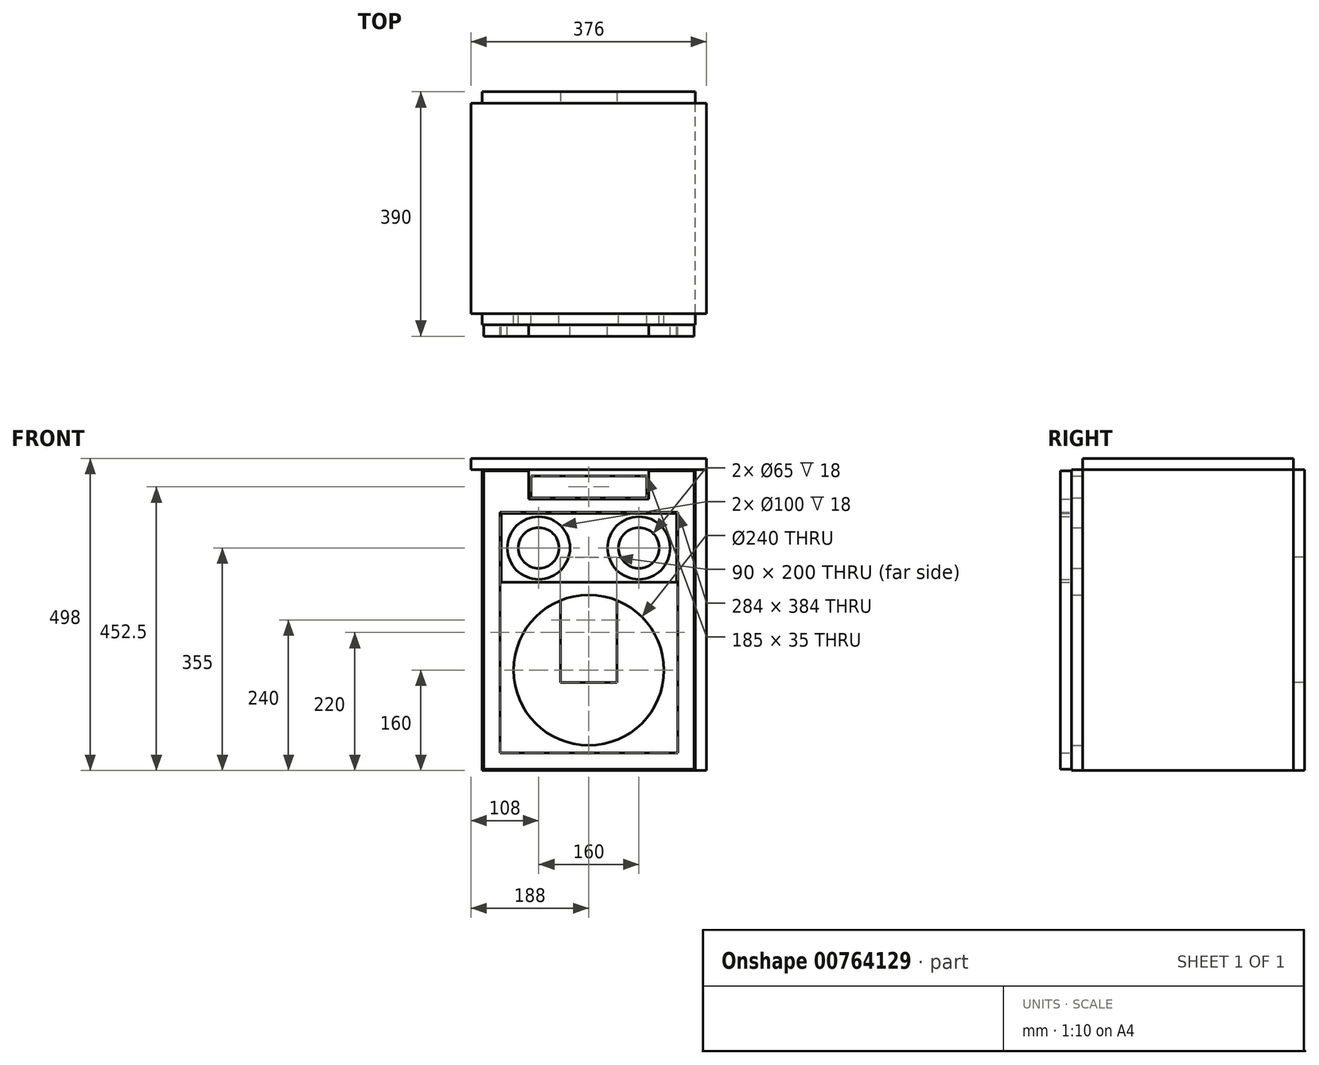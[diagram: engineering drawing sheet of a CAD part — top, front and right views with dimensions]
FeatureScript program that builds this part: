
annotation { "Feature Type Name" : "Feature", "Feature Type Description" : "" }
export const myFeature = defineFeature(function(context is Context, id is Id, definition is map)
    precondition{}
    {
        {
            var Q0;
            Q0=qCreatedBy(makeId("Front.planeOp"),FACE);
            var sketch = newSketch(context, id + "F0", { "sketchPlane" : qUnion([Q0])});
            skLineSegment(sketch, "E0.bottom", {"start": v(170, -240) * mm, "end": v(-170, -240) * mm});
            skLineSegment(sketch, "E0.top", {"start": v(170, 240) * mm, "end": v(-170, 240) * mm});
            skLineSegment(sketch, "E0.left", {"start": v(170, -240) * mm, "end": v(170, 240) * mm});
            skLineSegment(sketch, "E0.right", {"start": v(-170, -240) * mm, "end": v(-170, 240) * mm});
            skPoint(sketch, "E0.middle", {"position": v(0, 0) * mm});
            skLineSegment(sketch, "E1", {"start": v(0, 240) * mm, "end": v(0, -240) * mm, "construction": true});
            skCircle(sketch, "E2", {"center": v(0, -80) * mm, "radius": 120 * mm});
            skCircle(sketch, "E3", {"center": v(-80, 115) * mm, "radius": 32.5 * mm});
            skCircle(sketch, "E4", {"center": v(80, 115) * mm, "radius": 32.5 * mm});
            skLineSegment(sketch, "E5.bottom", {"start": v(92.5, 195) * mm, "end": v(-92.5, 195) * mm});
            skLineSegment(sketch, "E5.top", {"start": v(92.5, 230) * mm, "end": v(-92.5, 230) * mm});
            skLineSegment(sketch, "E5.left", {"start": v(92.5, 195) * mm, "end": v(92.5, 230) * mm});
            skLineSegment(sketch, "E5.right", {"start": v(-92.5, 195) * mm, "end": v(-92.5, 230) * mm});
            skPoint(sketch, "E5.middle", {"position": v(0, 212.5) * mm});
            skSolve(sketch);
        }
        {
            var Q0;
            Q0 = qSketchRegion(id + "F0", true);
            extrude(context, id + "F1", {"entities" : qUnion([Q0]), "depth" : 18 * mm, "offsetDistance" : 25 * mm});
        }
        {
            var Q0;
            Q0=makeQuery(id+"F1.opExtrude","CAP_FACE",FACE,{"disambiguationData":[OSD([sQuery(id+"F0.wireOp",EDGE,"E0.bottom"),sQuery(id+"F0.wireOp",EDGE,"E0.top"),sQuery(id+"F0.wireOp",EDGE,"E0.left"),sQuery(id+"F0.wireOp",EDGE,"E0.right"),sQuery(id+"F0.wireOp",EDGE,"E2")])],"isStart":false});
            var sketch = newSketch(context, id + "F2", { "sketchPlane" : qUnion([Q0])});
            skLineSegment(sketch, "E6.bottom", {"start": v(-140, 60) * mm, "end": v(140, 60) * mm});
            skLineSegment(sketch, "E6.top", {"start": v(-140, 170) * mm, "end": v(140, 170) * mm});
            skLineSegment(sketch, "E6.left", {"start": v(-140, 60) * mm, "end": v(-140, 170) * mm});
            skLineSegment(sketch, "E6.right", {"start": v(140, 60) * mm, "end": v(140, 170) * mm});
            skCircle(sketch, "E7", {"center": v(-80, 115) * mm, "radius": 50 * mm});
            skPoint(sketch, "E7.centerSnap0", {"position": v(-140, 115) * mm});
            skCircle(sketch, "E8", {"center": v(80, 115) * mm, "radius": 50 * mm});
            skPoint(sketch, "E8.centerSnap0", {"position": v(140, 115) * mm});
            skSolve(sketch);
        }
        {
            var Q0;
            Q0 = qSketchRegion(id + "F2", true);
            extrude(context, id + "F3", {"entities" : qUnion([Q0]), "operationType" : NewBodyOperationType.ADD, "depth" : 18 * mm, "offsetDistance" : 25 * mm});
        }
        {
            var Q0;
            Q0=makeQuery(id+"F1.opExtrude","CAP_FACE",FACE,{"disambiguationData":[OSD([sQuery(id+"F0.wireOp",EDGE,"E0.bottom"),sQuery(id+"F0.wireOp",EDGE,"E0.top"),sQuery(id+"F0.wireOp",EDGE,"E0.left"),sQuery(id+"F0.wireOp",EDGE,"E0.right"),sQuery(id+"F0.wireOp",EDGE,"E2"),sQuery(id+"F0.wireOp",EDGE,"E3"),sQuery(id+"F0.wireOp",EDGE,"E4")])],"isStart":false});
            var sketch = newSketch(context, id + "F4", { "sketchPlane" : qUnion([Q0])});
            skLineSegment(sketch, "E9.top", {"start": v(-168, -238) * mm, "end": v(168, -238) * mm});
            skLineSegment(sketch, "E9.left", {"start": v(-168, 238) * mm, "end": v(-168, -238) * mm});
            skLineSegment(sketch, "E9.right", {"start": v(168, 238) * mm, "end": v(168, -238) * mm});
            skLineSegment(sketch, "E10", {"start": v(-168, 238) * mm, "end": v(-96, 238) * mm});
            skLineSegment(sketch, "E11", {"start": v(-96, 238) * mm, "end": v(-96, 193) * mm});
            skLineSegment(sketch, "E12", {"start": v(-96, 193) * mm, "end": v(96, 193) * mm});
            skLineSegment(sketch, "E13", {"start": v(96, 193) * mm, "end": v(96, 238) * mm});
            skLineSegment(sketch, "E14", {"start": v(96, 238) * mm, "end": v(168, 238) * mm});
            skLineSegment(sketch, "E15.bottom", {"start": v(-142, 172) * mm, "end": v(142, 172) * mm});
            skLineSegment(sketch, "E15.top", {"start": v(-142, -212) * mm, "end": v(142, -212) * mm});
            skLineSegment(sketch, "E15.left", {"start": v(-142, 172) * mm, "end": v(-142, -212) * mm});
            skLineSegment(sketch, "E15.right", {"start": v(142, 172) * mm, "end": v(142, -212) * mm});
            skSolve(sketch);
        }
        {
            var Q0;
            Q0 = qSketchRegion(id + "F4", true);
            extrude(context, id + "F5", {"entities" : qUnion([Q0]), "depth" : 18 * mm, "offsetDistance" : 25 * mm});
        }
        {
            var Q0;
            Q0=makeQuery(id+"F1.opExtrude","SWEPT_FACE",FACE,{"disambiguationData":[OSD([sQuery(id+"F0.wireOp",EDGE,"E0.left")])]});
            var sketch = newSketch(context, id + "F6", { "sketchPlane" : qUnion([Q0])});
            skLineSegment(sketch, "E16.bottom", {"start": v(0, 240) * mm, "end": v(336, 240) * mm});
            skLineSegment(sketch, "E16.top", {"start": v(0, -240) * mm, "end": v(336, -240) * mm});
            skLineSegment(sketch, "E16.left", {"start": v(0, 240) * mm, "end": v(0, -240) * mm});
            skLineSegment(sketch, "E16.right", {"start": v(336, 240) * mm, "end": v(336, -240) * mm});
            skSolve(sketch);
        }
        {
            var Q0;
            Q0 = qSketchRegion(id + "F6", true);
            extrude(context, id + "F7", {"entities" : qUnion([Q0]), "depth" : 18 * mm, "offsetDistance" : 25 * mm});
        }
        {
            var Q0;
            Q0=makeQuery(id+"F1.opExtrude","CAP_FACE",FACE,{"disambiguationData":[OSD([sQuery(id+"F0.wireOp",EDGE,"E0.bottom"),sQuery(id+"F0.wireOp",EDGE,"E0.top"),sQuery(id+"F0.wireOp",EDGE,"E0.left"),sQuery(id+"F0.wireOp",EDGE,"E0.right"),sQuery(id+"F0.wireOp",EDGE,"E2"),sQuery(id+"F0.wireOp",EDGE,"E3"),sQuery(id+"F0.wireOp",EDGE,"E4")])],"isStart":true});
            var sketch = newSketch(context, id + "F8", { "sketchPlane" : qUnion([Q0])});
            skLineSegment(sketch, "E17.bottom", {"start": v(-170, 240) * mm, "end": v(170, 240) * mm});
            skLineSegment(sketch, "E17.top", {"start": v(-170, -240) * mm, "end": v(170, -240) * mm});
            skLineSegment(sketch, "E17.left", {"start": v(-170, 240) * mm, "end": v(-170, -240) * mm});
            skLineSegment(sketch, "E17.right", {"start": v(170, 240) * mm, "end": v(170, -240) * mm});
            skSolve(sketch);
        }
        {
            var Q0;
            Q0 = qSketchRegion(id + "F8", true);
            extrude(context, id + "F9", {"entities" : qUnion([Q0]), "depth" : 18 * mm, "offsetDistance" : 25 * mm});
        }
        {
            var Q0;
            Q0=makeQuery(id+"F9.opExtrude","SWEPT_BODY",BODY,{"disambiguationData":[OSD([sQuery(id+"F8.wireOp",EDGE,"E17.bottom"),sQuery(id+"F8.wireOp",EDGE,"E17.top"),sQuery(id+"F8.wireOp",EDGE,"E17.left"),sQuery(id+"F8.wireOp",EDGE,"E17.right")])]});
            deleteBodies(context, id + "F10", {"entities" : qUnion([Q0])});
        }
        {
            var Q0;
            Q0=makeQuery(id+"F7.opExtrude","SWEPT_FACE",FACE,{"disambiguationData":[OSD([sQuery(id+"F6.wireOp",EDGE,"E16.right")])]});
            var sketch = newSketch(context, id + "F11", { "sketchPlane" : qUnion([Q0])});
            skLineSegment(sketch, "E18.bottom", {"start": v(-170, 240) * mm, "end": v(170, 240) * mm});
            skLineSegment(sketch, "E18.top", {"start": v(-170, -240) * mm, "end": v(170, -240) * mm});
            skLineSegment(sketch, "E18.left", {"start": v(-170, 240) * mm, "end": v(-170, -240) * mm});
            skLineSegment(sketch, "E18.right", {"start": v(170, 240) * mm, "end": v(170, -240) * mm});
            skLineSegment(sketch, "E19", {"start": v(0, 240) * mm, "end": v(0, -240) * mm, "construction": true});
            skLineSegment(sketch, "E20", {"start": v(-162.43, 0) * mm, "end": v(170, 0) * mm, "construction": true});
            skPoint(sketch, "E20.startSnap0", {"position": v(-170, 0) * mm});
            skLineSegment(sketch, "E21", {"start": v(170, 0) * mm, "end": v(172.71, -3.77) * mm, "construction": true});
            skPoint(sketch, "E22.middle", {"position": v(0, 0) * mm});
            skLineSegment(sketch, "E23.bottom", {"start": v(45, -100) * mm, "end": v(-45, -100) * mm});
            skLineSegment(sketch, "E23.top", {"start": v(45, 100) * mm, "end": v(-45, 100) * mm});
            skLineSegment(sketch, "E23.left", {"start": v(45, -100) * mm, "end": v(45, 100) * mm});
            skLineSegment(sketch, "E23.right", {"start": v(-45, -100) * mm, "end": v(-45, 100) * mm});
            skSolve(sketch);
        }
        {
            var Q0;
            Q0 = qSketchRegion(id + "F11", true);
            extrude(context, id + "F12", {"entities" : qUnion([Q0]), "depth" : 18 * mm, "offsetDistance" : 25 * mm});
        }
        {
            var Q0;
            Q0=makeQuery(id+"F7.opExtrude","SWEPT_FACE",FACE,{"disambiguationData":[OSD([sQuery(id+"F6.wireOp",EDGE,"E16.bottom")])]});
            var sketch = newSketch(context, id + "F13", { "sketchPlane" : qUnion([Q0])});
            skLineSegment(sketch, "E24.bottom", {"start": v(188, 0) * mm, "end": v(-188, 0) * mm});
            skLineSegment(sketch, "E24.top", {"start": v(188, 336) * mm, "end": v(-188, 336) * mm});
            skLineSegment(sketch, "E24.left", {"start": v(188, 0) * mm, "end": v(188, 336) * mm});
            skLineSegment(sketch, "E24.right", {"start": v(-188, 0) * mm, "end": v(-188, 336) * mm});
            skSolve(sketch);
        }
        {
            var Q0;
            Q0 = qSketchRegion(id + "F13", true);
            extrude(context, id + "F14", {"entities" : qUnion([Q0]), "depth" : 18 * mm, "offsetDistance" : 25 * mm});
        }
    });
